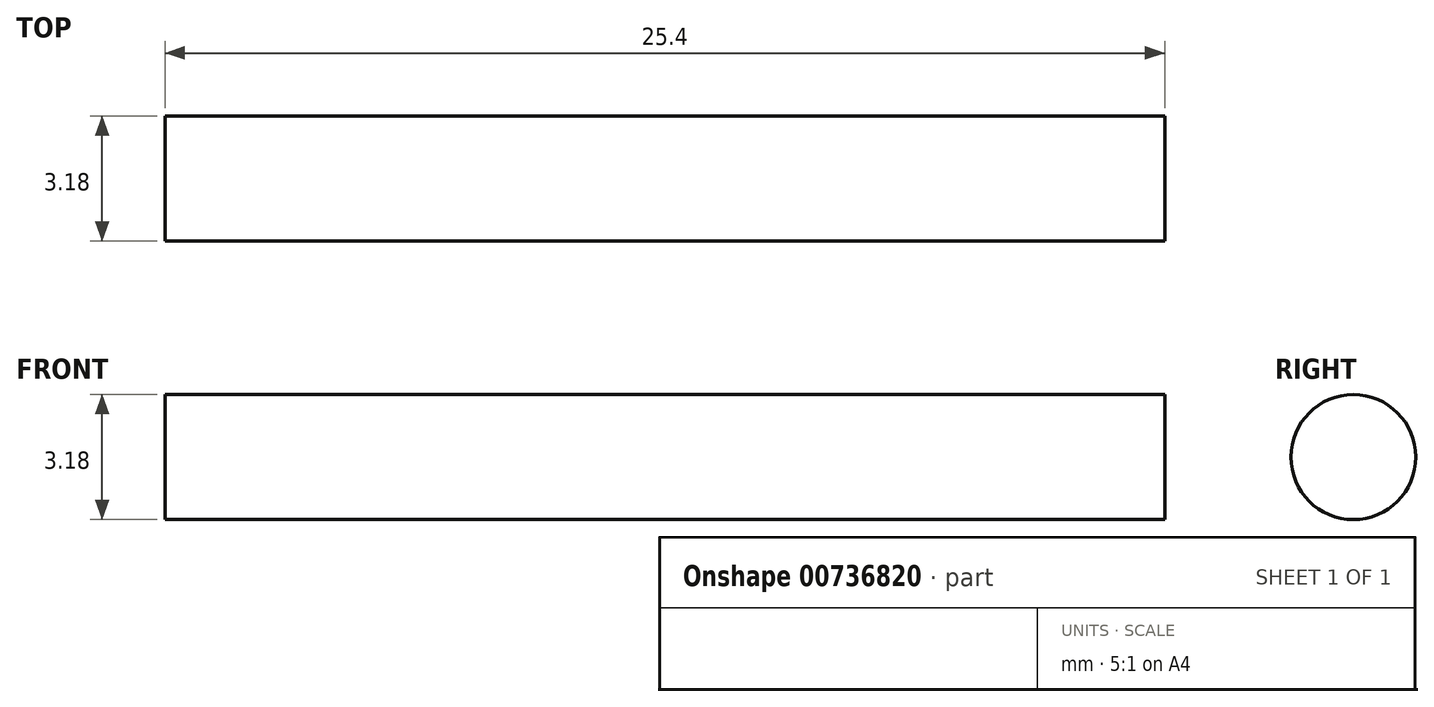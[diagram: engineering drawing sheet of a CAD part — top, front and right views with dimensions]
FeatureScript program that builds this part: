
annotation { "Feature Type Name" : "Feature", "Feature Type Description" : "" }
export const myFeature = defineFeature(function(context is Context, id is Id, definition is map)
    precondition{}
    {
        {
            var Q0;
            Q0=qCreatedBy(makeId("Right.planeOp"),FACE);
            var sketch = newSketch(context, id + "F0", { "sketchPlane" : qUnion([Q0])});
            skCircle(sketch, "E0", {"center": v(0, 0) * mm, "radius": 1.59 * mm});
            skSolve(sketch);
        }
        {
            var Q0;
            Q0=makeQuery(id+"F0.imprint","IMPRINT",FACE,{"disambiguationData":[TD([[makeQuery(id+"F0.imprint","IMPRINT",EDGE,{"derivedFrom":sQuery(id+"F0.wireOp",EDGE,"E0")}),1.0]])]});
            extrude(context, id + "F1", {"entities" : qUnion([Q0]), "depth" : 25.4 * mm, "offsetDistance" : 25.4 * mm});
        }
    });
